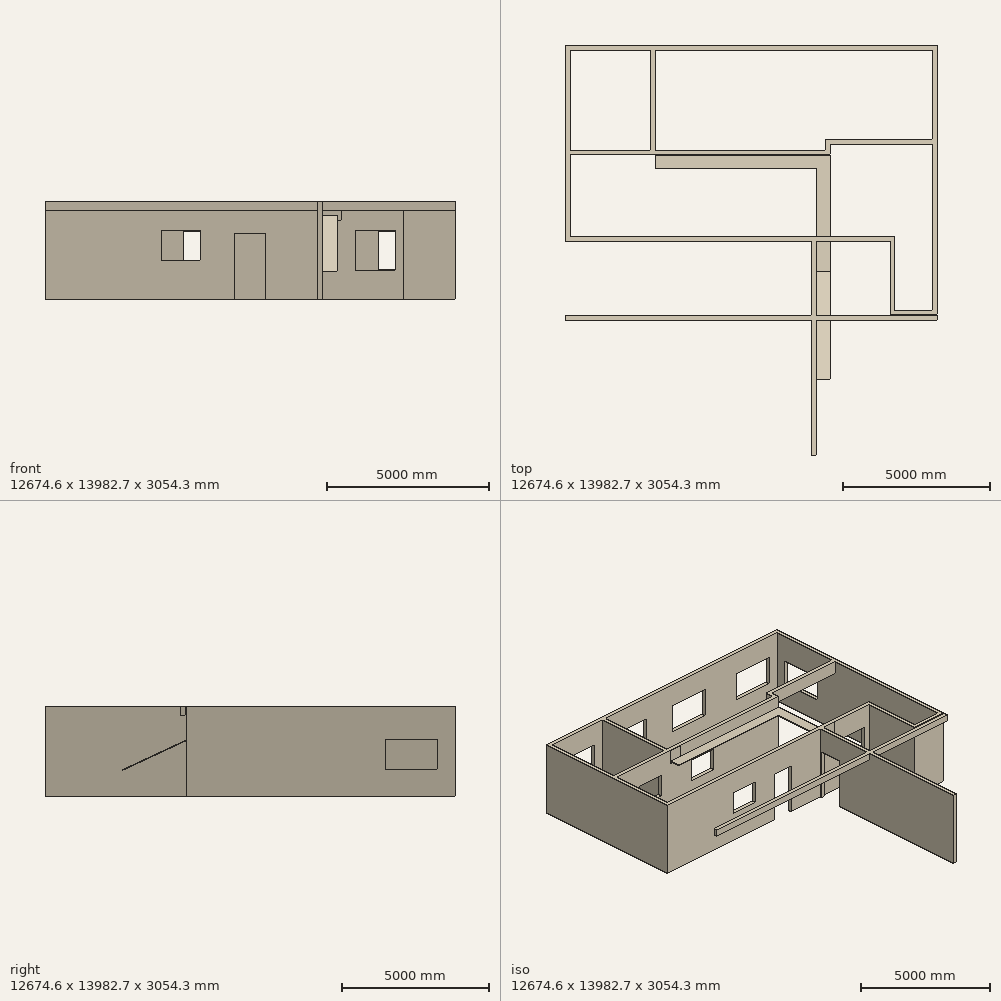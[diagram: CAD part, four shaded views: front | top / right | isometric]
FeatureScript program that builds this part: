
annotation { "Feature Type Name" : "Feature", "Feature Type Description" : "" }
export const myFeature = defineFeature(function(context is Context, id is Id, definition is map)
    precondition{}
    {
        {
            var Q0;
            Q0=qCreatedBy(makeId("Top.planeOp"),FACE);
            var sketch = newSketch(context, id + "F0", { "sketchPlane" : qUnion([Q0])});
            skLineSegment(sketch, "E0.bottom", {"start": v(-8071.83, 2939.2) * mm, "end": v(-5328.63, 2939.2) * mm});
            skLineSegment(sketch, "E0.top", {"start": v(-8071.83, -3398.1) * mm, "end": v(-2394.93, -3398.1) * mm});
            skLineSegment(sketch, "E0.left", {"start": v(-8071.83, 2939.2) * mm, "end": v(-8071.83, -464.4) * mm});
            skLineSegment(sketch, "E0.right", {"start": v(4272.57, 2939.2) * mm, "end": v(4272.57, 48.64) * mm});
            skLineSegment(sketch, "E1", {"start": v(640.37, -464.4) * mm, "end": v(640.37, 48.64) * mm, "construction": true});
            skLineSegment(sketch, "E2", {"start": v(-7157.43, -464.4) * mm, "end": v(-8071.83, -464.4) * mm, "construction": true});
            skLineSegment(sketch, "E3", {"start": v(-5328.63, 2939.2) * mm, "end": v(-5328.63, -464.4) * mm});
            skLineSegment(sketch, "E4", {"start": v(640.37, 48.64) * mm, "end": v(2443.77, 48.64) * mm, "construction": true});
            skLineSegment(sketch, "E5", {"start": v(2443.77, 48.64) * mm, "end": v(4272.57, 48.64) * mm, "construction": true});
            skLineSegment(sketch, "E6", {"start": v(-8071.83, -629.5) * mm, "end": v(-7157.43, -629.5) * mm, "construction": true});
            skLineSegment(sketch, "E7", {"start": v(-7157.43, -629.5) * mm, "end": v(-5163.53, -629.5) * mm});
            skLineSegment(sketch, "E8", {"start": v(805.47, -464.4) * mm, "end": v(805.47, -116.46) * mm, "construction": true});
            skLineSegment(sketch, "E9", {"start": v(805.47, -116.46) * mm, "end": v(2443.77, -116.46) * mm, "construction": true});
            skLineSegment(sketch, "E10", {"start": v(2443.77, -116.46) * mm, "end": v(4272.57, -116.46) * mm, "construction": true});
            skLineSegment(sketch, "E11.bottom", {"start": v(-8236.93, 3104.3) * mm, "end": v(4437.67, 3104.3) * mm});
            skLineSegment(sketch, "E11.top", {"start": v(-8236.93, -3563.2) * mm, "end": v(-2394.93, -3563.2) * mm});
            skLineSegment(sketch, "E11.left", {"start": v(-8236.93, 3104.3) * mm, "end": v(-8236.93, -3563.2) * mm});
            skLineSegment(sketch, "E11.right", {"start": v(4437.67, 3104.3) * mm, "end": v(4437.67, -3398.1) * mm});
            skLineSegment(sketch, "E12", {"start": v(-5163.53, 2939.2) * mm, "end": v(-5163.53, -464.4) * mm});
            skLineSegment(sketch, "E13.trimOffspring", {"start": v(-8071.83, -629.5) * mm, "end": v(-8071.83, -3398.1) * mm});
            skLineSegment(sketch, "E14.trimOffspring", {"start": v(4272.57, -116.46) * mm, "end": v(4272.57, -3398.1) * mm});
            skLineSegment(sketch, "E15.trimOffspring", {"start": v(-5328.63, -464.4) * mm, "end": v(-7157.43, -464.4) * mm});
            skLineSegment(sketch, "E16.trimOffspring", {"start": v(-5163.53, 2939.2) * mm, "end": v(4272.57, 2939.2) * mm});
            skLineSegment(sketch, "E17", {"start": v(-7157.43, -464.4) * mm, "end": v(-7157.43, -629.5) * mm});
            skLineSegment(sketch, "E18", {"start": v(-8071.83, -464.4) * mm, "end": v(-8071.83, -629.5) * mm});
            skLineSegment(sketch, "E19", {"start": v(2443.77, 48.64) * mm, "end": v(2443.77, -116.46) * mm, "construction": true});
            skLineSegment(sketch, "E20", {"start": v(4272.57, 48.64) * mm, "end": v(4272.57, -116.46) * mm});
            skLineSegment(sketch, "E21", {"start": v(640.37, -464.4) * mm, "end": v(-4249.13, -464.4) * mm});
            skLineSegment(sketch, "E22", {"start": v(-4249.13, -464.4) * mm, "end": v(-5163.53, -464.4) * mm});
            skLineSegment(sketch, "E23", {"start": v(-4249.13, -464.4) * mm, "end": v(-4249.13, -629.5) * mm, "construction": true});
            skLineSegment(sketch, "E24", {"start": v(-5163.53, -464.4) * mm, "end": v(-5163.53, -629.5) * mm, "construction": true});
            skLineSegment(sketch, "E25.trimOffspring", {"start": v(-4249.13, -629.5) * mm, "end": v(805.47, -629.5) * mm});
            skLineSegment(sketch, "E26", {"start": v(-5163.53, -629.5) * mm, "end": v(-4249.13, -629.5) * mm});
            skLineSegment(sketch, "E27", {"start": v(640.37, -464.4) * mm, "end": v(805.47, -464.4) * mm});
            skLineSegment(sketch, "E28", {"start": v(805.47, -629.5) * mm, "end": v(805.47, -464.4) * mm});
            skLineSegment(sketch, "E29", {"start": v(2831.12, -3563.2) * mm, "end": v(2831.12, -6074.84) * mm});
            skLineSegment(sketch, "E30", {"start": v(2831.12, -6074.84) * mm, "end": v(4437.67, -6074.84) * mm});
            skLineSegment(sketch, "E31", {"start": v(4437.67, -6074.84) * mm, "end": v(4437.67, -3398.1) * mm});
            skLineSegment(sketch, "E32", {"start": v(4272.57, -3398.1) * mm, "end": v(4272.57, -5922.44) * mm});
            skLineSegment(sketch, "E33", {"start": v(4272.57, -5922.44) * mm, "end": v(2983.52, -5922.44) * mm});
            skLineSegment(sketch, "E34", {"start": v(2983.52, -5922.44) * mm, "end": v(2983.52, -3398.1) * mm});
            skLineSegment(sketch, "E35", {"start": v(-1442.43, -3398.1) * mm, "end": v(-1442.43, -3563.2) * mm});
            skLineSegment(sketch, "E36", {"start": v(-2394.93, -3398.1) * mm, "end": v(-2394.93, -3563.2) * mm});
            skLineSegment(sketch, "E37.trimOffspring", {"start": v(-1442.43, -3563.2) * mm, "end": v(157.77, -3563.2) * mm});
            skLineSegment(sketch, "E38", {"start": v(157.77, -3563.2) * mm, "end": v(157.77, -10878.4) * mm});
            skLineSegment(sketch, "E39", {"start": v(157.77, -10878.4) * mm, "end": v(322.87, -10878.4) * mm});
            skLineSegment(sketch, "E40", {"start": v(322.87, -10878.4) * mm, "end": v(322.87, -3563.2) * mm});
            skLineSegment(sketch, "E41.trimOffspring", {"start": v(322.87, -3563.2) * mm, "end": v(2831.12, -3563.2) * mm});
            skLineSegment(sketch, "E42", {"start": v(-1442.43, -3398.1) * mm, "end": v(2983.52, -3398.1) * mm});
            skSolve(sketch);
        }
        {
            var Q0;
            Q0=makeQuery(id+"F0.imprint","IMPRINT",FACE,{"disambiguationData":[TD([[makeQuery(id+"F0.imprint","IMPRINT",EDGE,{"derivedFrom":sQuery(id+"F0.wireOp",EDGE,"E0.bottom")}),1.0]])]});
            var Q1;
            Q1=makeQuery(id+"F0.imprint","IMPRINT",FACE,{"disambiguationData":[TD([[makeQuery(id+"F0.imprint","IMPRINT",EDGE,{"derivedFrom":sQuery(id+"F0.wireOp",EDGE,"E1")}),-1.0]])]});
            extrude(context, id + "F1", {"entities" : qUnion([Q0, Q1]), "depth" : 3054.35 * mm, "offsetDistance" : 25.4 * mm});
        }
        {
            var Q0;
            Q0=makeQuery(id+"F1.opExtrude","SWEPT_FACE",FACE,{"disambiguationData":[OSD([sQuery(id+"F0.wireOp",EDGE,"E7")])]});
            var sketch = newSketch(context, id + "F2", { "sketchPlane" : qUnion([Q0])});
            skLineSegment(sketch, "E43.bottom", {"start": v(-6852.63, 2133.6) * mm, "end": v(-5633.43, 2133.6) * mm});
            skLineSegment(sketch, "E43.top", {"start": v(-6852.63, 1219.2) * mm, "end": v(-5633.43, 1219.2) * mm});
            skLineSegment(sketch, "E43.left", {"start": v(-6852.63, 2133.6) * mm, "end": v(-6852.63, 1219.2) * mm});
            skLineSegment(sketch, "E43.right", {"start": v(-5633.43, 2133.6) * mm, "end": v(-5633.43, 1219.2) * mm});
            skLineSegment(sketch, "E44.bottom", {"start": v(-3982.43, 2133.6) * mm, "end": v(-2763.23, 2133.6) * mm});
            skLineSegment(sketch, "E44.top", {"start": v(-3982.43, 1219.2) * mm, "end": v(-2763.23, 1219.2) * mm});
            skLineSegment(sketch, "E44.left", {"start": v(-3982.43, 2133.6) * mm, "end": v(-3982.43, 1219.2) * mm});
            skLineSegment(sketch, "E44.right", {"start": v(-2763.23, 2133.6) * mm, "end": v(-2763.23, 1219.2) * mm});
            skSolve(sketch);
        }
        {
            var Q0;
            Q0 = qSketchRegion(id + "F2", true);
            extrude(context, id + "F3", {"entities" : qUnion([Q0]), "operationType" : NewBodyOperationType.REMOVE, "endBound" : BoundingType.UP_TO_NEXT, "oppositeDirection" : true, "depth" : 25.4 * mm, "offsetDistance" : 25.4 * mm});
        }
        {
            var Q0;
            Q0=makeQuery(id+"F1.opExtrude","SWEPT_FACE",FACE,{"disambiguationData":[OSD([sQuery(id+"F0.wireOp",EDGE,"E0.bottom")])]});
            var sketch = newSketch(context, id + "F4", { "sketchPlane" : qUnion([Q0])});
            skLineSegment(sketch, "E45.bottom", {"start": v(-7525.73, 2108.2) * mm, "end": v(-5747.73, 2108.2) * mm});
            skLineSegment(sketch, "E45.top", {"start": v(-7525.73, 927.1) * mm, "end": v(-5747.73, 927.1) * mm});
            skLineSegment(sketch, "E45.left", {"start": v(-7525.73, 2108.2) * mm, "end": v(-7525.73, 927.1) * mm});
            skLineSegment(sketch, "E45.right", {"start": v(-5747.73, 2108.2) * mm, "end": v(-5747.73, 927.1) * mm});
            skLineSegment(sketch, "E46.bottom", {"start": v(-4680.93, 2108.2) * mm, "end": v(-2902.93, 2108.2) * mm});
            skLineSegment(sketch, "E46.top", {"start": v(-4680.93, 927.1) * mm, "end": v(-2902.93, 927.1) * mm});
            skLineSegment(sketch, "E46.left", {"start": v(-4680.93, 2108.2) * mm, "end": v(-4680.93, 927.1) * mm});
            skLineSegment(sketch, "E46.right", {"start": v(-2902.93, 2108.2) * mm, "end": v(-2902.93, 927.1) * mm});
            skLineSegment(sketch, "E47.bottom", {"start": v(-1455.13, 2108.2) * mm, "end": v(322.87, 2108.2) * mm});
            skLineSegment(sketch, "E47.top", {"start": v(-1455.13, 927.1) * mm, "end": v(322.87, 927.1) * mm});
            skLineSegment(sketch, "E47.left", {"start": v(-1455.13, 2108.2) * mm, "end": v(-1455.13, 927.1) * mm});
            skLineSegment(sketch, "E47.right", {"start": v(322.87, 2108.2) * mm, "end": v(322.87, 927.1) * mm});
            skLineSegment(sketch, "E48.bottom", {"start": v(2062.77, 2108.2) * mm, "end": v(3840.77, 2108.2) * mm});
            skLineSegment(sketch, "E48.top", {"start": v(2062.77, 927.1) * mm, "end": v(3840.77, 927.1) * mm});
            skLineSegment(sketch, "E48.left", {"start": v(2062.77, 2108.2) * mm, "end": v(2062.77, 927.1) * mm});
            skLineSegment(sketch, "E48.right", {"start": v(3840.77, 2108.2) * mm, "end": v(3840.77, 927.1) * mm});
            skSolve(sketch);
        }
        {
            var Q0;
            Q0 = qSketchRegion(id + "F4", true);
            extrude(context, id + "F5", {"entities" : qUnion([Q0]), "operationType" : NewBodyOperationType.REMOVE, "endBound" : BoundingType.THROUGH_ALL, "oppositeDirection" : true, "depth" : 25.4 * mm, "offsetDistance" : 25.4 * mm});
        }
        {
            var Q0;
            Q0=makeQuery(id+"F1.opExtrude","SWEPT_FACE",FACE,{"disambiguationData":[OSD([sQuery(id+"F0.wireOp",EDGE,"E0.right"),sQuery(id+"F0.wireOp",EDGE,"E14.trimOffspring"),sQuery(id+"F0.wireOp",EDGE,"E20")])]});
            var sketch = newSketch(context, id + "F6", { "sketchPlane" : qUnion([Q0])});
            skLineSegment(sketch, "E49.bottom", {"start": v(-2507.4, 1943.1) * mm, "end": v(-729.4, 1943.1) * mm});
            skLineSegment(sketch, "E49.top", {"start": v(-2507.4, 927.1) * mm, "end": v(-729.4, 927.1) * mm});
            skLineSegment(sketch, "E49.left", {"start": v(-2507.4, 1943.1) * mm, "end": v(-2507.4, 927.1) * mm});
            skLineSegment(sketch, "E49.right", {"start": v(-729.4, 1943.1) * mm, "end": v(-729.4, 927.1) * mm});
            skSolve(sketch);
        }
        {
            var Q0;
            Q0 = qSketchRegion(id + "F6", true);
            extrude(context, id + "F7", {"entities" : qUnion([Q0]), "operationType" : NewBodyOperationType.REMOVE, "endBound" : BoundingType.THROUGH_ALL, "oppositeDirection" : true, "depth" : 25.4 * mm, "offsetDistance" : 25.4 * mm});
        }
        {
            var Q0;
            Q0=qCreatedBy(makeId("Top.planeOp"),FACE);
            cPlane(context, id + "F8", {"entities" : qUnion([Q0]), "cplaneType" : CPlaneType.OFFSET, "offset" : 2533.65 * mm, "width" : 152.4 * mm, "height" : 152.4 * mm});
        }
        {
            var Q0;
            Q0=qCreatedBy(id+"F8.planeOp",FACE);
            var sketch = newSketch(context, id + "F9", { "sketchPlane" : qUnion([Q0])});
            skLineSegment(sketch, "E50.bottom", {"start": v(640.37, -464.4) * mm, "end": v(-5163.53, -464.4) * mm});
            skLineSegment(sketch, "E50.top", {"start": v(4272.57, 2939.2) * mm, "end": v(-5163.53, 2939.2) * mm});
            skLineSegment(sketch, "E50.left", {"start": v(4272.57, -87.2) * mm, "end": v(4272.57, 2939.2) * mm});
            skLineSegment(sketch, "E50.right", {"start": v(-5163.53, -464.4) * mm, "end": v(-5163.53, 2939.2) * mm});
            skLineSegment(sketch, "E51.bottom", {"start": v(-8071.83, 2939.2) * mm, "end": v(-5163.53, 2939.2) * mm});
            skLineSegment(sketch, "E51.top", {"start": v(-8071.83, -464.4) * mm, "end": v(-5163.53, -464.4) * mm});
            skLineSegment(sketch, "E51.left", {"start": v(-8071.83, 2939.2) * mm, "end": v(-8071.83, -464.4) * mm});
            skLineSegment(sketch, "E51.right", {"start": v(-5163.53, 2939.2) * mm, "end": v(-5163.53, -464.4) * mm});
            skLineSegment(sketch, "E52", {"start": v(640.37, -464.4) * mm, "end": v(640.37, -87.2) * mm});
            skLineSegment(sketch, "E53", {"start": v(640.37, -87.2) * mm, "end": v(4272.57, -87.2) * mm});
            skSolve(sketch);
        }
        {
            var Q0;
            Q0=qCreatedBy(makeId("Top.planeOp"),FACE);
            var sketch = newSketch(context, id + "F10", { "sketchPlane" : qUnion([Q0])});
            skLineSegment(sketch, "E54.bottom", {"start": v(640.37, -96.1) * mm, "end": v(4272.57, -96.1) * mm});
            skLineSegment(sketch, "E54.top", {"start": v(805.47, -261.2) * mm, "end": v(4272.57, -261.2) * mm});
            skLineSegment(sketch, "E54.right", {"start": v(4272.57, -96.1) * mm, "end": v(4272.57, -261.2) * mm});
            skLineSegment(sketch, "E55", {"start": v(805.47, -261.2) * mm, "end": v(805.47, -464.4) * mm});
            skLineSegment(sketch, "E56", {"start": v(640.37, -96.1) * mm, "end": v(640.37, -464.4) * mm});
            skLineSegment(sketch, "E57", {"start": v(640.37, -464.4) * mm, "end": v(805.47, -464.4) * mm});
            skSolve(sketch);
        }
        {
            var Q0;
            Q0 = qSketchRegion(id + "F10", true);
            var Q1;
            Q1=makeQuery(id+"F1.opExtrude","CAP_FACE",FACE,{"disambiguationData":[OSD([sQuery(id+"F0.wireOp",EDGE,"E0.bottom"),sQuery(id+"F0.wireOp",EDGE,"E0.top"),sQuery(id+"F0.wireOp",EDGE,"E0.left"),sQuery(id+"F0.wireOp",EDGE,"E0.right"),sQuery(id+"F0.wireOp",EDGE,"E3"),sQuery(id+"F0.wireOp",EDGE,"E7"),sQuery(id+"F0.wireOp",EDGE,"E11.bottom"),sQuery(id+"F0.wireOp",EDGE,"E11.top"),sQuery(id+"F0.wireOp",EDGE,"E11.left"),sQuery(id+"F0.wireOp",EDGE,"E11.right"),sQuery(id+"F0.wireOp",EDGE,"E12"),sQuery(id+"F0.wireOp",EDGE,"E13.trimOffspring"),sQuery(id+"F0.wireOp",EDGE,"E14.trimOffspring"),sQuery(id+"F0.wireOp",EDGE,"E15.trimOffspring"),sQuery(id+"F0.wireOp",EDGE,"E16.trimOffspring"),sQuery(id+"F0.wireOp",EDGE,"E17"),sQuery(id+"F0.wireOp",EDGE,"E18"),sQuery(id+"F0.wireOp",EDGE,"E20"),sQuery(id+"F0.wireOp",EDGE,"E21"),sQuery(id+"F0.wireOp",EDGE,"E22"),sQuery(id+"F0.wireOp",EDGE,"E25.trimOffspring"),sQuery(id+"F0.wireOp",EDGE,"E26"),sQuery(id+"F0.wireOp",EDGE,"E27"),sQuery(id+"F0.wireOp",EDGE,"E28")])],"isStart":false});
            extrude(context, id + "F11", {"entities" : qUnion([Q0]), "endBound" : BoundingType.UP_TO_SURFACE, "depth" : 25.4 * mm, "endBoundEntityFace" : qUnion([Q1]), "offsetDistance" : 25.4 * mm});
        }
        {
            var Q0;
            Q0=makeQuery(id+"F11.opExtrude","SWEPT_FACE",FACE,{"disambiguationData":[OSD([sQuery(id+"F10.wireOp",EDGE,"E54.top")])]});
            var sketch = newSketch(context, id + "F12", { "sketchPlane" : qUnion([Q0])});
            skLineSegment(sketch, "E58.bottom", {"start": v(805.47, 2514.6) * mm, "end": v(4272.57, 2514.6) * mm});
            skLineSegment(sketch, "E58.top", {"start": v(805.47, 0) * mm, "end": v(4272.57, 0) * mm});
            skLineSegment(sketch, "E58.left", {"start": v(805.47, 2514.6) * mm, "end": v(805.47, 0) * mm});
            skLineSegment(sketch, "E58.right", {"start": v(4272.57, 2514.6) * mm, "end": v(4272.57, 0) * mm});
            skSolve(sketch);
        }
        {
            var Q0;
            Q0 = qSketchRegion(id + "F12", true);
            extrude(context, id + "F13", {"entities" : qUnion([Q0]), "operationType" : NewBodyOperationType.REMOVE, "endBound" : BoundingType.UP_TO_NEXT, "oppositeDirection" : true, "depth" : 25.4 * mm, "offsetDistance" : 25.4 * mm});
        }
        {
            var Q0;
            Q0=makeQuery(id+"F1.opExtrude","SWEPT_FACE",FACE,{"disambiguationData":[OSD([sQuery(id+"F0.wireOp",EDGE,"E38")])]});
            var sketch = newSketch(context, id + "F14", { "sketchPlane" : qUnion([Q0])});
            skLineSegment(sketch, "E59.bottom", {"start": v(3639.4, 2044.7) * mm, "end": v(4591.9, 2044.7) * mm});
            skLineSegment(sketch, "E59.top", {"start": v(3639.4, 0) * mm, "end": v(4591.9, 0) * mm});
            skLineSegment(sketch, "E59.left", {"start": v(3639.4, 2044.7) * mm, "end": v(3639.4, 0) * mm});
            skLineSegment(sketch, "E59.right", {"start": v(4591.9, 2044.7) * mm, "end": v(4591.9, 0) * mm});
            skSolve(sketch);
        }
        {
            var Q0;
            Q0 = qSketchRegion(id + "F14", true);
            extrude(context, id + "F15", {"entities" : qUnion([Q0]), "operationType" : NewBodyOperationType.REMOVE, "endBound" : BoundingType.UP_TO_NEXT, "oppositeDirection" : true, "depth" : 25.4 * mm, "offsetDistance" : 25.4 * mm});
        }
        {
            var Q0;
            Q0=makeQuery(id+"F1.opExtrude","SWEPT_FACE",FACE,{"disambiguationData":[OSD([sQuery(id+"F0.wireOp",EDGE,"E7"),sQuery(id+"F0.wireOp",EDGE,"E25.trimOffspring"),sQuery(id+"F0.wireOp",EDGE,"E26")])]});
            var sketch = newSketch(context, id + "F16", { "sketchPlane" : qUnion([Q0])});
            skPoint(sketch, "E60.oppositeSnap0", {"position": v(-7157.43, 2044.7) * mm});
            skLineSegment(sketch, "E60.bottom", {"start": v(-7157.43, 3054.35) * mm, "end": v(-8071.83, 3054.35) * mm});
            skLineSegment(sketch, "E60.top", {"start": v(-7157.43, 2044.7) * mm, "end": v(-8071.83, 2044.7) * mm});
            skLineSegment(sketch, "E60.left", {"start": v(-7157.43, 3054.35) * mm, "end": v(-7157.43, 2044.7) * mm});
            skLineSegment(sketch, "E60.right", {"start": v(-8071.83, 3054.35) * mm, "end": v(-8071.83, 2044.7) * mm});
            skSolve(sketch);
        }
        {
            var Q0;
            Q0 = qSketchRegion(id + "F16", true);
            extrude(context, id + "F17", {"entities" : qUnion([Q0]), "operationType" : NewBodyOperationType.ADD, "oppositeDirection" : true, "depth" : 165.1 * mm, "offsetDistance" : 25.4 * mm});
        }
        {
            var Q0;
            Q0=makeQuery(id+"F1.opExtrude","SWEPT_FACE",FACE,{"disambiguationData":[OSD([sQuery(id+"F0.wireOp",EDGE,"E11.top")])]});
            var sketch = newSketch(context, id + "F18", { "sketchPlane" : qUnion([Q0])});
            skLineSegment(sketch, "E61.bottom", {"start": v(-2394.93, 3054.35) * mm, "end": v(-1442.43, 3054.35) * mm});
            skLineSegment(sketch, "E61.top", {"start": v(-2394.93, 2044.7) * mm, "end": v(-1442.43, 2044.7) * mm});
            skLineSegment(sketch, "E61.left", {"start": v(-2394.93, 3054.35) * mm, "end": v(-2394.93, 2044.7) * mm});
            skLineSegment(sketch, "E61.right", {"start": v(-1442.43, 3054.35) * mm, "end": v(-1442.43, 2044.7) * mm});
            skSolve(sketch);
        }
        {
            var Q0;
            Q0 = qSketchRegion(id + "F18", true);
            extrude(context, id + "F19", {"entities" : qUnion([Q0]), "operationType" : NewBodyOperationType.ADD, "oppositeDirection" : true, "depth" : 165.1 * mm, "offsetDistance" : 25.4 * mm});
        }
        {
            var Q0;
            Q0=makeQuery(id+"F19.boolean.opBoolean","MERGE",FACE,{"derivedFrom":[makeQuery(id+"F17.boolean.opBoolean","MERGE",FACE,{"derivedFrom":[makeQuery(id+"F1.opExtrude","CAP_FACE",FACE,{"disambiguationData":[OSD([sQuery(id+"F0.wireOp",EDGE,"E0.bottom"),sQuery(id+"F0.wireOp",EDGE,"E0.top"),sQuery(id+"F0.wireOp",EDGE,"E0.left"),sQuery(id+"F0.wireOp",EDGE,"E0.right"),sQuery(id+"F0.wireOp",EDGE,"E3"),sQuery(id+"F0.wireOp",EDGE,"E7"),sQuery(id+"F0.wireOp",EDGE,"E11.bottom"),sQuery(id+"F0.wireOp",EDGE,"E11.top"),sQuery(id+"F0.wireOp",EDGE,"E11.left"),sQuery(id+"F0.wireOp",EDGE,"E11.right"),sQuery(id+"F0.wireOp",EDGE,"E12"),sQuery(id+"F0.wireOp",EDGE,"E13.trimOffspring"),sQuery(id+"F0.wireOp",EDGE,"E14.trimOffspring"),sQuery(id+"F0.wireOp",EDGE,"E15.trimOffspring"),sQuery(id+"F0.wireOp",EDGE,"E16.trimOffspring"),sQuery(id+"F0.wireOp",EDGE,"E17"),sQuery(id+"F0.wireOp",EDGE,"E18"),sQuery(id+"F0.wireOp",EDGE,"E20"),sQuery(id+"F0.wireOp",EDGE,"E21"),sQuery(id+"F0.wireOp",EDGE,"E22"),sQuery(id+"F0.wireOp",EDGE,"E25.trimOffspring"),sQuery(id+"F0.wireOp",EDGE,"E26"),sQuery(id+"F0.wireOp",EDGE,"E27"),sQuery(id+"F0.wireOp",EDGE,"E28"),sQuery(id+"F0.wireOp",EDGE,"E29"),sQuery(id+"F0.wireOp",EDGE,"E30"),sQuery(id+"F0.wireOp",EDGE,"E31"),sQuery(id+"F0.wireOp",EDGE,"E32"),sQuery(id+"F0.wireOp",EDGE,"E33"),sQuery(id+"F0.wireOp",EDGE,"E34"),sQuery(id+"F0.wireOp",EDGE,"E35"),sQuery(id+"F0.wireOp",EDGE,"E36"),sQuery(id+"F0.wireOp",EDGE,"E37.trimOffspring"),sQuery(id+"F0.wireOp",EDGE,"E38"),sQuery(id+"F0.wireOp",EDGE,"E39"),sQuery(id+"F0.wireOp",EDGE,"E40"),sQuery(id+"F0.wireOp",EDGE,"E41.trimOffspring"),sQuery(id+"F0.wireOp",EDGE,"E42")])],"isStart":false}),makeQuery(id+"F17.opExtrude","SWEPT_FACE",FACE,{"disambiguationData":[OSD([sQuery(id+"F16.wireOp",EDGE,"E60.bottom")])]})]}),makeQuery(id+"F19.opExtrude","SWEPT_FACE",FACE,{"disambiguationData":[OSD([sQuery(id+"F18.wireOp",EDGE,"E61.bottom")])]})]});
            var sketch = newSketch(context, id + "F20", { "sketchPlane" : qUnion([Q0])});
            skLineSegment(sketch, "E62.bottom", {"start": v(-8236.93, -6115.9) * mm, "end": v(4437.67, -6115.9) * mm});
            skLineSegment(sketch, "E62.top", {"start": v(-8236.93, -6268.3) * mm, "end": v(4437.67, -6268.3) * mm});
            skLineSegment(sketch, "E62.left", {"start": v(-8236.93, -6115.9) * mm, "end": v(-8236.93, -6268.3) * mm});
            skLineSegment(sketch, "E62.right", {"start": v(4437.67, -6115.9) * mm, "end": v(4437.67, -6268.3) * mm});
            skLineSegment(sketch, "E63", {"start": v(4437.67, -6115.9) * mm, "end": v(4437.67, -6074.84) * mm, "construction": true});
            skLineSegment(sketch, "E64", {"start": v(-8236.93, -6115.9) * mm, "end": v(-8236.93, -3563.2) * mm});
            skSolve(sketch);
        }
        {
            var Q0;
            Q0 = qSketchRegion(id + "F20", true);
            extrude(context, id + "F21", {"entities" : qUnion([Q0]), "operationType" : NewBodyOperationType.ADD, "oppositeDirection" : true, "depth" : 285.75 * mm, "offsetDistance" : 25.4 * mm});
        }
        {
            var Q0;
            Q0=makeQuery(id+"F1.opExtrude","SWEPT_FACE",FACE,{"disambiguationData":[OSD([sQuery(id+"F0.wireOp",EDGE,"E41.trimOffspring")])]});
            var sketch = newSketch(context, id + "F22", { "sketchPlane" : qUnion([Q0])});
            skLineSegment(sketch, "E65.bottom", {"start": v(1357.92, 2133.6) * mm, "end": v(2577.12, 2133.6) * mm});
            skLineSegment(sketch, "E65.top", {"start": v(1357.92, 914.4) * mm, "end": v(2577.12, 914.4) * mm});
            skLineSegment(sketch, "E65.left", {"start": v(1357.92, 2133.6) * mm, "end": v(1357.92, 914.4) * mm});
            skLineSegment(sketch, "E65.right", {"start": v(2577.12, 2133.6) * mm, "end": v(2577.12, 914.4) * mm});
            skLineSegment(sketch, "E66.bottom", {"start": v(-4649.18, 2133.6) * mm, "end": v(-3429.98, 2133.6) * mm});
            skLineSegment(sketch, "E66.top", {"start": v(-4649.18, 1219.2) * mm, "end": v(-3429.98, 1219.2) * mm});
            skLineSegment(sketch, "E66.left", {"start": v(-4649.18, 2133.6) * mm, "end": v(-4649.18, 1219.2) * mm});
            skLineSegment(sketch, "E66.right", {"start": v(-3429.98, 2133.6) * mm, "end": v(-3429.98, 1219.2) * mm});
            skSolve(sketch);
        }
        {
            var Q0;
            Q0 = qSketchRegion(id + "F22", true);
            extrude(context, id + "F23", {"entities" : qUnion([Q0]), "operationType" : NewBodyOperationType.REMOVE, "endBound" : BoundingType.UP_TO_NEXT, "oppositeDirection" : true, "depth" : 25.4 * mm, "offsetDistance" : 25.4 * mm});
        }
        {
            var Q0;
            Q0=makeQuery(id+"F13.boolean.opBoolean","MERGE",FACE,{"derivedFrom":[makeQuery(id+"F11.opExtrude","SWEPT_FACE",FACE,{"disambiguationData":[OSD([sQuery(id+"F10.wireOp",EDGE,"E55")])]}),makeQuery(id+"F13.opExtrude","SWEPT_FACE",FACE,{"disambiguationData":[OSD([sQuery(id+"F12.wireOp",EDGE,"E58.left")])]})]});
            var sketch = newSketch(context, id + "F24", { "sketchPlane" : qUnion([Q0])});
            skLineSegment(sketch, "E67.bottom", {"start": v(-464.4, 2514.6) * mm, "end": v(-96.1, 2514.6) * mm});
            skLineSegment(sketch, "E67.left", {"start": v(-464.4, 2514.6) * mm, "end": v(-464.4, 0) * mm});
            skLineSegment(sketch, "E67.right", {"start": v(-96.1, 2514.6) * mm, "end": v(-96.1, 0) * mm});
            skLineSegment(sketch, "E68", {"start": v(-464.4, 0) * mm, "end": v(-96.1, 0) * mm});
            skSolve(sketch);
        }
        {
            var Q0;
            Q0 = qSketchRegion(id + "F24", true);
            extrude(context, id + "F25", {"entities" : qUnion([Q0]), "operationType" : NewBodyOperationType.REMOVE, "endBound" : BoundingType.UP_TO_NEXT, "oppositeDirection" : true, "depth" : 25.4 * mm, "offsetDistance" : 25.4 * mm});
        }
        {
            var Q0;
            Q0=makeQuery(id+"F25.boolean.opBoolean","MERGE",FACE,{"derivedFrom":[makeQuery(id+"F13.boolean.opBoolean","COPY",FACE,{"derivedFrom":makeQuery(id+"F13.opExtrude","SWEPT_FACE",FACE,{"disambiguationData":[OSD([sQuery(id+"F12.wireOp",EDGE,"E58.bottom")])]})}),makeQuery(id+"F25.opExtrude","SWEPT_FACE",FACE,{"disambiguationData":[OSD([sQuery(id+"F24.wireOp",EDGE,"E67.bottom")])]})]});
            var sketch = newSketch(context, id + "F26", { "sketchPlane" : qUnion([Q0])});
            skLineSegment(sketch, "E69.bottom", {"start": v(805.47, 464.4) * mm, "end": v(640.37, 464.4) * mm});
            skLineSegment(sketch, "E69.top", {"start": v(805.47, 261.2) * mm, "end": v(640.37, 261.2) * mm});
            skLineSegment(sketch, "E69.left", {"start": v(805.47, 464.4) * mm, "end": v(805.47, 261.2) * mm});
            skLineSegment(sketch, "E69.right", {"start": v(640.37, 464.4) * mm, "end": v(640.37, 261.2) * mm});
            skSolve(sketch);
        }
        {
            var Q0;
            Q0 = qSketchRegion(id + "F26", true);
            var Q1;
            {var subQ0=sQuery(id+"F0.wireOp",EDGE,"E35");var subQ1=sQuery(id+"F0.wireOp",EDGE,"E34");var subQ2=sQuery(id+"F0.wireOp",EDGE,"E33");var subQ3=sQuery(id+"F0.wireOp",EDGE,"E30");var subQ4=sQuery(id+"F0.wireOp",EDGE,"E29");var subQ5=sQuery(id+"F0.wireOp",EDGE,"E28");var subQ6=sQuery(id+"F0.wireOp",EDGE,"E27");var subQ7=sQuery(id+"F0.wireOp",EDGE,"E22");var subQ8=sQuery(id+"F0.wireOp",EDGE,"E21");var subQ9=sQuery(id+"F0.wireOp",EDGE,"E17");var subQ10=sQuery(id+"F0.wireOp",EDGE,"E16.trimOffspring");var subQ11=sQuery(id+"F0.wireOp",EDGE,"E15.trimOffspring");var subQ12=sQuery(id+"F0.wireOp",EDGE,"E12");var subQ13=sQuery(id+"F0.wireOp",EDGE,"E18");var subQ14=sQuery(id+"F0.wireOp",EDGE,"E13.trimOffspring");var subQ15=sQuery(id+"F0.wireOp",EDGE,"E0.left");var subQ16=sQuery(id+"F0.wireOp",EDGE,"E0.top");var subQ17=sQuery(id+"F0.wireOp",EDGE,"E32");var subQ18=sQuery(id+"F0.wireOp",EDGE,"E20");var subQ19=sQuery(id+"F0.wireOp",EDGE,"E14.trimOffspring");var subQ20=sQuery(id+"F0.wireOp",EDGE,"E0.right");var subQ21=sQuery(id+"F0.wireOp",EDGE,"E36");var subQ22=sQuery(id+"F0.wireOp",EDGE,"E0.bottom");var subQ23=sQuery(id+"F0.wireOp",EDGE,"E31");var subQ24=sQuery(id+"F0.wireOp",EDGE,"E11.right");var subQ25=sQuery(id+"F0.wireOp",EDGE,"E3");var subQ26=sQuery(id+"F0.wireOp",EDGE,"E26");var subQ27=sQuery(id+"F0.wireOp",EDGE,"E25.trimOffspring");var subQ28=sQuery(id+"F0.wireOp",EDGE,"E7");var subQ29=sQuery(id+"F0.wireOp",EDGE,"E11.bottom");var subQ30=sQuery(id+"F0.wireOp",EDGE,"E11.top");var subQ31=sQuery(id+"F0.wireOp",EDGE,"E11.left");var subQ32=sQuery(id+"F0.wireOp",EDGE,"E37.trimOffspring");var subQ33=sQuery(id+"F0.wireOp",EDGE,"E38");var subQ34=sQuery(id+"F0.wireOp",EDGE,"E40");var subQ35=sQuery(id+"F0.wireOp",EDGE,"E41.trimOffspring");var subQ36=sQuery(id+"F0.wireOp",EDGE,"E42");Q1=makeQuery(id+"F15.boolean.opBoolean","SPLIT",FACE,{"disambiguationData":[TD([makeQuery(id+"F1.opExtrude","SWEPT_FACE",FACE,{"disambiguationData":[OSD([subQ22])]})])],"derivedFrom":makeQuery(id+"F1.opExtrude","CAP_FACE",FACE,{"disambiguationData":[OSD([subQ22,subQ16,subQ15,subQ20,subQ25,subQ28,subQ29,subQ30,subQ31,subQ24,subQ12,subQ14,subQ19,subQ11,subQ10,subQ9,subQ13,subQ18,subQ8,subQ7,subQ27,subQ26,subQ6,subQ5,subQ4,subQ3,subQ23,subQ17,subQ2,subQ1,subQ0,subQ21,subQ32,subQ33,sQuery(id+"F0.wireOp",EDGE,"E39"),subQ34,subQ35,subQ36])],"isStart":true})});}
            extrude(context, id + "F27", {"entities" : qUnion([Q0]), "operationType" : NewBodyOperationType.ADD, "endBound" : BoundingType.UP_TO_SURFACE, "depth" : 25.4 * mm, "endBoundEntityFace" : qUnion([Q1]), "offsetDistance" : 25.4 * mm});
        }
        {
            var Q0;
            {var subQ0=sQuery(id+"F0.wireOp",EDGE,"E42");var subQ1=sQuery(id+"F0.wireOp",EDGE,"E41.trimOffspring");var subQ2=sQuery(id+"F0.wireOp",EDGE,"E40");var subQ3=sQuery(id+"F0.wireOp",EDGE,"E39");var subQ4=sQuery(id+"F0.wireOp",EDGE,"E38");var subQ5=sQuery(id+"F0.wireOp",EDGE,"E37.trimOffspring");var subQ6=sQuery(id+"F0.wireOp",EDGE,"E36");var subQ7=sQuery(id+"F0.wireOp",EDGE,"E35");var subQ8=sQuery(id+"F0.wireOp",EDGE,"E34");var subQ9=sQuery(id+"F0.wireOp",EDGE,"E33");var subQ10=sQuery(id+"F0.wireOp",EDGE,"E32");var subQ11=sQuery(id+"F0.wireOp",EDGE,"E31");var subQ12=sQuery(id+"F0.wireOp",EDGE,"E30");var subQ13=sQuery(id+"F0.wireOp",EDGE,"E29");var subQ14=sQuery(id+"F0.wireOp",EDGE,"E28");var subQ15=sQuery(id+"F0.wireOp",EDGE,"E27");var subQ16=sQuery(id+"F0.wireOp",EDGE,"E26");var subQ17=sQuery(id+"F0.wireOp",EDGE,"E25.trimOffspring");var subQ18=sQuery(id+"F0.wireOp",EDGE,"E22");var subQ19=sQuery(id+"F0.wireOp",EDGE,"E21");var subQ20=sQuery(id+"F0.wireOp",EDGE,"E20");var subQ21=sQuery(id+"F0.wireOp",EDGE,"E18");var subQ22=sQuery(id+"F0.wireOp",EDGE,"E17");var subQ23=sQuery(id+"F0.wireOp",EDGE,"E16.trimOffspring");var subQ24=sQuery(id+"F0.wireOp",EDGE,"E15.trimOffspring");var subQ25=sQuery(id+"F0.wireOp",EDGE,"E14.trimOffspring");var subQ26=sQuery(id+"F0.wireOp",EDGE,"E13.trimOffspring");var subQ27=sQuery(id+"F0.wireOp",EDGE,"E12");var subQ28=sQuery(id+"F0.wireOp",EDGE,"E11.right");var subQ29=sQuery(id+"F0.wireOp",EDGE,"E11.left");var subQ30=sQuery(id+"F0.wireOp",EDGE,"E11.top");var subQ31=sQuery(id+"F0.wireOp",EDGE,"E11.bottom");var subQ32=sQuery(id+"F0.wireOp",EDGE,"E7");var subQ33=sQuery(id+"F0.wireOp",EDGE,"E3");var subQ34=sQuery(id+"F0.wireOp",EDGE,"E0.right");var subQ35=sQuery(id+"F0.wireOp",EDGE,"E0.left");var subQ36=sQuery(id+"F0.wireOp",EDGE,"E0.top");var subQ37=sQuery(id+"F0.wireOp",EDGE,"E0.bottom");Q0=makeQuery(id+"F27.boolean.opBoolean","MERGE",FACE,{"derivedFrom":[makeQuery(id+"F11.opExtrude","CAP_FACE",FACE,{"disambiguationData":[OSD([subQ37,subQ36,subQ35,subQ34,subQ33,subQ32,subQ31,subQ30,subQ29,subQ28,subQ27,subQ26,subQ25,subQ24,subQ23,subQ22,subQ21,subQ20,subQ19,subQ18,subQ17,subQ16,subQ15,subQ14,subQ13,subQ12,subQ11,subQ10,subQ9,subQ8,subQ7,subQ6,subQ5,subQ4,subQ3,subQ2,subQ1,subQ0])],"isStart":false}),makeQuery(id+"F21.boolean.opBoolean","MERGE",FACE,{"derivedFrom":[makeQuery(id+"F19.boolean.opBoolean","MERGE",FACE,{"derivedFrom":[makeQuery(id+"F17.boolean.opBoolean","MERGE",FACE,{"derivedFrom":[makeQuery(id+"F1.opExtrude","CAP_FACE",FACE,{"disambiguationData":[OSD([subQ37,subQ36,subQ35,subQ34,subQ33,subQ32,subQ31,subQ30,subQ29,subQ28,subQ27,subQ26,subQ25,subQ24,subQ23,subQ22,subQ21,subQ20,subQ19,subQ18,subQ17,subQ16,subQ15,subQ14,subQ13,subQ12,subQ11,subQ10,subQ9,subQ8,subQ7,subQ6,subQ5,subQ4,subQ3,subQ2,subQ1,subQ0])],"isStart":false}),makeQuery(id+"F17.opExtrude","SWEPT_FACE",FACE,{"disambiguationData":[OSD([sQuery(id+"F16.wireOp",EDGE,"E60.bottom")])]})]}),makeQuery(id+"F19.opExtrude","SWEPT_FACE",FACE,{"disambiguationData":[OSD([sQuery(id+"F18.wireOp",EDGE,"E61.bottom")])]})]}),makeQuery(id+"F21.opExtrude","CAP_FACE",FACE,{"disambiguationData":[OSD([sQuery(id+"F20.wireOp",EDGE,"E62.bottom"),sQuery(id+"F20.wireOp",EDGE,"E62.top"),sQuery(id+"F20.wireOp",EDGE,"E62.left"),sQuery(id+"F20.wireOp",EDGE,"E62.right")])],"isStart":true})]})]});}
            cPlane(context, id + "F28", {"entities" : qUnion([Q0]), "cplaneType" : CPlaneType.OFFSET, "offset" : 457.2 * mm, "oppositeDirection" : true, "width" : 152.4 * mm, "height" : 152.4 * mm});
        }
        {
            var Q0;
            Q0=qCreatedBy(id+"F28.planeOp",FACE);
            var sketch = newSketch(context, id + "F29", { "sketchPlane" : qUnion([Q0])});
            skLineSegment(sketch, "E70.bottom", {"start": v(-5163.53, -649.6) * mm, "end": v(322.87, -649.6) * mm});
            skLineSegment(sketch, "E70.top", {"start": v(-5163.53, -1106.8) * mm, "end": v(322.87, -1106.8) * mm});
            skLineSegment(sketch, "E70.left", {"start": v(-5163.53, -649.6) * mm, "end": v(-5163.53, -1106.8) * mm});
            skLineSegment(sketch, "E71.bottom", {"start": v(322.87, -649.6) * mm, "end": v(780.07, -649.6) * mm});
            skLineSegment(sketch, "E71.top", {"start": v(322.87, -4612) * mm, "end": v(780.07, -4612) * mm});
            skLineSegment(sketch, "E71.left", {"start": v(322.87, -1106.8) * mm, "end": v(322.87, -4612) * mm});
            skLineSegment(sketch, "E71.right", {"start": v(780.07, -649.6) * mm, "end": v(780.07, -4612) * mm});
            skSolve(sketch);
        }
        {
            var Q0;
            Q0 = qSketchRegion(id + "F29", true);
            extrude(context, id + "F30", {"entities" : qUnion([Q0]), "oppositeDirection" : true, "depth" : 25.4 * mm, "offsetDistance" : 25.4 * mm});
        }
        {
            var Q0;
            Q0=makeQuery(id+"F1.opExtrude","SWEPT_FACE",FACE,{"disambiguationData":[OSD([sQuery(id+"F0.wireOp",EDGE,"E40")])]});
            var sketch = newSketch(context, id + "F31", { "sketchPlane" : qUnion([Q0])});
            skLineSegment(sketch, "E72", {"start": v(-4612, 2571.75) * mm, "end": v(-8275.13, 863.6) * mm});
            skLineSegment(sketch, "E73", {"start": v(-4612, 2597.15) * mm, "end": v(-8275.13, 889) * mm});
            skLineSegment(sketch, "E74", {"start": v(-4612, 2597.15) * mm, "end": v(-4612, 2571.75) * mm});
            skLineSegment(sketch, "E75", {"start": v(-4612, 2597.15) * mm, "end": v(-5848.35, 2597.15) * mm, "construction": true});
            skLineSegment(sketch, "E76", {"start": v(-8275.13, 863.6) * mm, "end": v(-8275.13, 889) * mm});
            skSolve(sketch);
        }
        {
            var Q0;
            Q0 = qSketchRegion(id + "F31", true);
            extrude(context, id + "F32", {"entities" : qUnion([Q0]), "depth" : 457.2 * mm, "offsetDistance" : 25.4 * mm});
        }
        {
            var Q0;
            Q0=makeQuery(id+"F1.opExtrude","SWEPT_FACE",FACE,{"disambiguationData":[OSD([sQuery(id+"F0.wireOp",EDGE,"E41.trimOffspring")])]});
            var sketch = newSketch(context, id + "F33", { "sketchPlane" : qUnion([Q0])});
            skLineSegment(sketch, "E77.bottom", {"start": v(322.87, 3054.35) * mm, "end": v(911.75, 3054.35) * mm});
            skLineSegment(sketch, "E77.top", {"start": v(322.87, 2440.32) * mm, "end": v(911.75, 2440.32) * mm});
            skLineSegment(sketch, "E77.left", {"start": v(322.87, 3054.35) * mm, "end": v(322.87, 2440.32) * mm});
            skLineSegment(sketch, "E77.right", {"start": v(911.75, 3054.35) * mm, "end": v(911.75, 2440.32) * mm});
            skSolve(sketch);
        }
        {
            var Q0;
            Q0 = qSketchRegion(id + "F33", true);
            extrude(context, id + "F34", {"entities" : qUnion([Q0]), "depth" : 2.54 * mm, "offsetDistance" : 25.4 * mm});
        }
        {
            var Q0;
            Q0=makeQuery(id+"F17.boolean.opBoolean","MERGE",FACE,{"derivedFrom":[makeQuery(id+"F1.opExtrude","SWEPT_FACE",FACE,{"disambiguationData":[OSD([sQuery(id+"F0.wireOp",EDGE,"E7"),sQuery(id+"F0.wireOp",EDGE,"E25.trimOffspring"),sQuery(id+"F0.wireOp",EDGE,"E26")])]}),makeQuery(id+"F17.opExtrude","CAP_FACE",FACE,{"disambiguationData":[OSD([sQuery(id+"F16.wireOp",EDGE,"E60.bottom"),sQuery(id+"F16.wireOp",EDGE,"E60.top"),sQuery(id+"F16.wireOp",EDGE,"E60.left"),sQuery(id+"F16.wireOp",EDGE,"E60.right")])],"isStart":true})]});
            var sketch = newSketch(context, id + "F35", { "sketchPlane" : qUnion([Q0])});
            skLineSegment(sketch, "E78.bottom", {"start": v(-5163.53, 3054.35) * mm, "end": v(-4581.78, 3054.35) * mm});
            skLineSegment(sketch, "E78.top", {"start": v(-5163.53, 2463.7) * mm, "end": v(-4581.78, 2463.7) * mm});
            skLineSegment(sketch, "E78.left", {"start": v(-5163.53, 3054.35) * mm, "end": v(-5163.53, 2463.7) * mm});
            skLineSegment(sketch, "E78.right", {"start": v(-4581.78, 3054.35) * mm, "end": v(-4581.78, 2463.7) * mm});
            skSolve(sketch);
        }
        {
            var Q0;
            Q0 = qSketchRegion(id + "F35", true);
            extrude(context, id + "F36", {"entities" : qUnion([Q0]), "depth" : 2.54 * mm, "offsetDistance" : 25.4 * mm});
        }
    });
